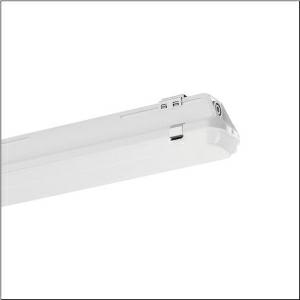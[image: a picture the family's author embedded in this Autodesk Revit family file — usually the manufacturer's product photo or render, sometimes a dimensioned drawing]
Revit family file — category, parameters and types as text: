
# Revit family: monsun_r__11_parking_51fg207p440h_0f51
name_source: partatom
category: Lighting Fixtures
units: mm (PartAtom-declared; Revit-internal decimal feet)

## family parameters
Cut with Voids When Loaded = No
Host = Face
Light Source = No
Part Type = Normal
Room Calculation Point = No
Round Connector Dimension = Use Diameter
Shared = No

## types (1)
- Monsun® 11 parking (1 x LED, 4820 lm, 29.2 W, 4000K)
    Apparent Load = 29 VA
    CIE Flux Codes = 45 75 93 94 100
    Color Rendering = 80
    Color Temperature = 4000K
    Default Elevation = 1800 mm
    Description = Monsun® 11 parking, damp-proof luminaire, chain hanger, primary optical cover: enclosure, of PC, light emission: direct distribution, primary light characteristic: symmetric, installation type: suspended mounting, surface-mounted, horizontal mounting, vertical mounting, LED, rated luminous flux: 4.820lm, luminous efficacy: 165lm/W, light colour: 840, colour temperature: 4000K, control gear: ON/OFF, with terminal, 3-pole, max. 2.5mm², mains connection: 220..240V, AC, 50/60Hz, rated input power: 29W, housing, of glass-fibre reinforced polyester, uncoated, bright grey, incl. chain hanger, length: 1.590mm, width: 90mm, height: 88mm, clip for enclosure, of stainless steel (V2A), ceiling mounting element, of stainless steel (V2A), chain hanger, of stainless steel (V2A), protection rating (complete): IP66, insulation class (complete): insulation class I (protective earthing), certification: CE, ENEC, VDE, UKCA, protection symbol: D, impact resistance: IK08, permissible operating ambient temperature: -35..+40°C, standard: EN 50419, EN 60598-2-1, no direct snow, no direct sun, no direct rain, for indoor or canopied outdoor use, corresponds to IFS (International Featured Standards) requirements for safety and quality in the food industry, contact your sales advisor before using the luminaires in applications with unclear chemical exposure, large temperature fluctuations or condensation-forming humidity, LABS conformity tested according to VDMA 24364:2018-05, packaging unit: 1 piece
    Height = 89 mm
    Lamp = 1 x LED
    Lamp Light Flux = 4820 lm
    Lamp Power = 29.2 W
    Lamp count = 1
    Length = 1590 mm
    Luminous efficacy = 165 lm/W
    Manufacturer = Siteco
    ModVariant = No
    Model = 51FG207P440H
    Mounting Place = Ceiling
    Mounting Type = Surface mounted
    Number of Poles = 1
    OnlyDefault = Yes
    Power Factor = 1
    Product Name = Monsun® 11 parking
    Product group = damp-proof luminaire
    ProductGroupID = 300
    Protection Class = Protection class I
    Protection Degree = IP 66
    RLX_Detail_Level = 1
    RLX_Emergency_Light_Flux = 0 lm
    RLX_Emergency_Type = 0
    RLX_Emergency_Type_DB = No
    RlxData = <blob elided: 88677 chars, md5=c8b5c3e1>
    Socket = socket
    Standby Power = 0 W
    System Light Flux = 4820 lm
    System Power = 29 W
    Type Comments = Product without accessories
    Type Image = l_1349237.jpg
    URL = http://relux.com
    VarID = ---
    Voltage = 0 V
    Weight = 0.00 kg
    Width = 90 mm

## geometry (parser evidence)
native form markers: Blend x4, Sweep x13
no freeform markers — native parametric forms only
